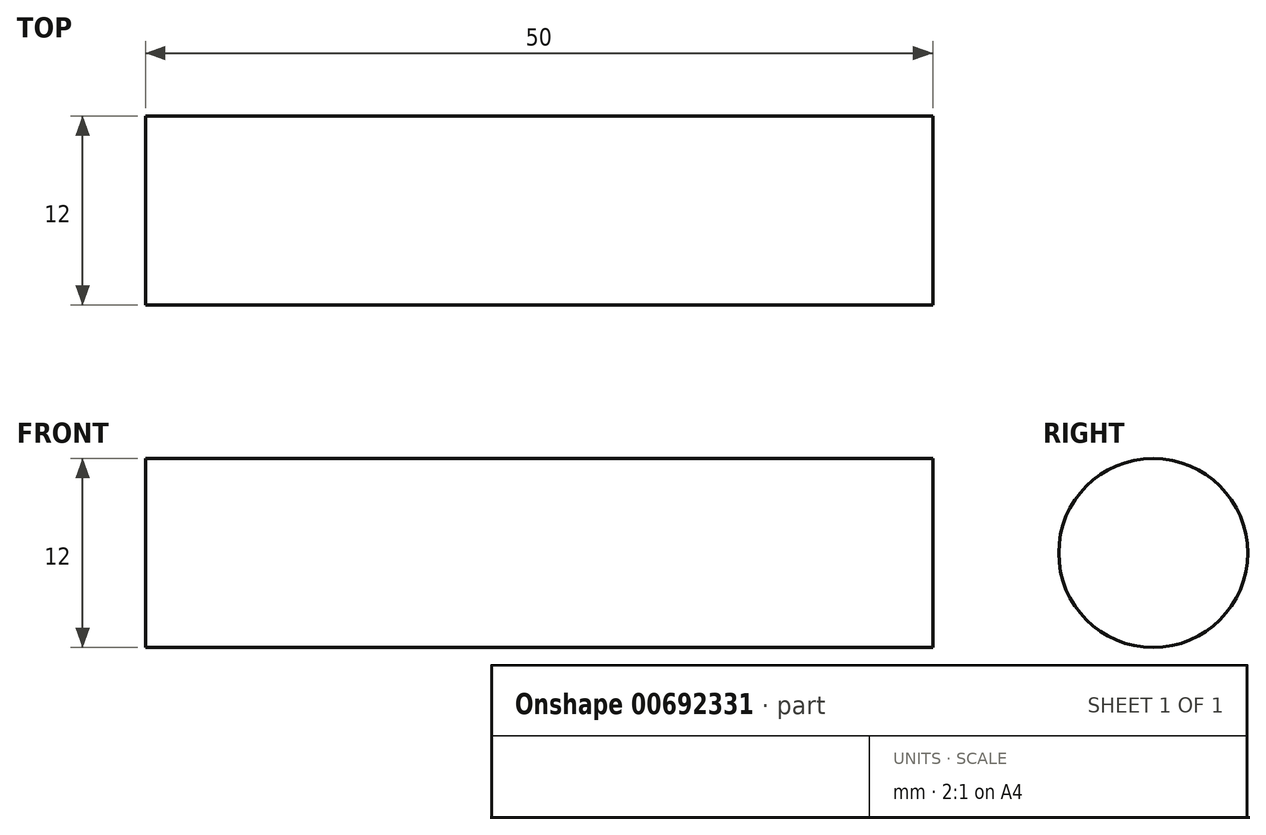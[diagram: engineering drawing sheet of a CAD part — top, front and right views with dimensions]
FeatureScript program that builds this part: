
annotation { "Feature Type Name" : "Feature", "Feature Type Description" : "" }
export const myFeature = defineFeature(function(context is Context, id is Id, definition is map)
    precondition{}
    {
        {
            var Q0;
            Q0=qCreatedBy(makeId("Right.planeOp"),FACE);
            var sketch = newSketch(context, id + "F0", { "sketchPlane" : qUnion([Q0])});
            skCircle(sketch, "E0", {"center": v(0, 0) * mm, "radius": 6 * mm});
            skSolve(sketch);
        }
        {
            var Q0;
            Q0=makeQuery(id+"F0.imprint","IMPRINT",FACE,{"disambiguationData":[TD([[makeQuery(id+"F0.imprint","IMPRINT",EDGE,{"derivedFrom":sQuery(id+"F0.wireOp",EDGE,"E0")}),1.0]])]});
            extrude(context, id + "F1", {"entities" : qUnion([Q0]), "depth" : 50 * mm, "offsetDistance" : 25 * mm});
        }
    });
